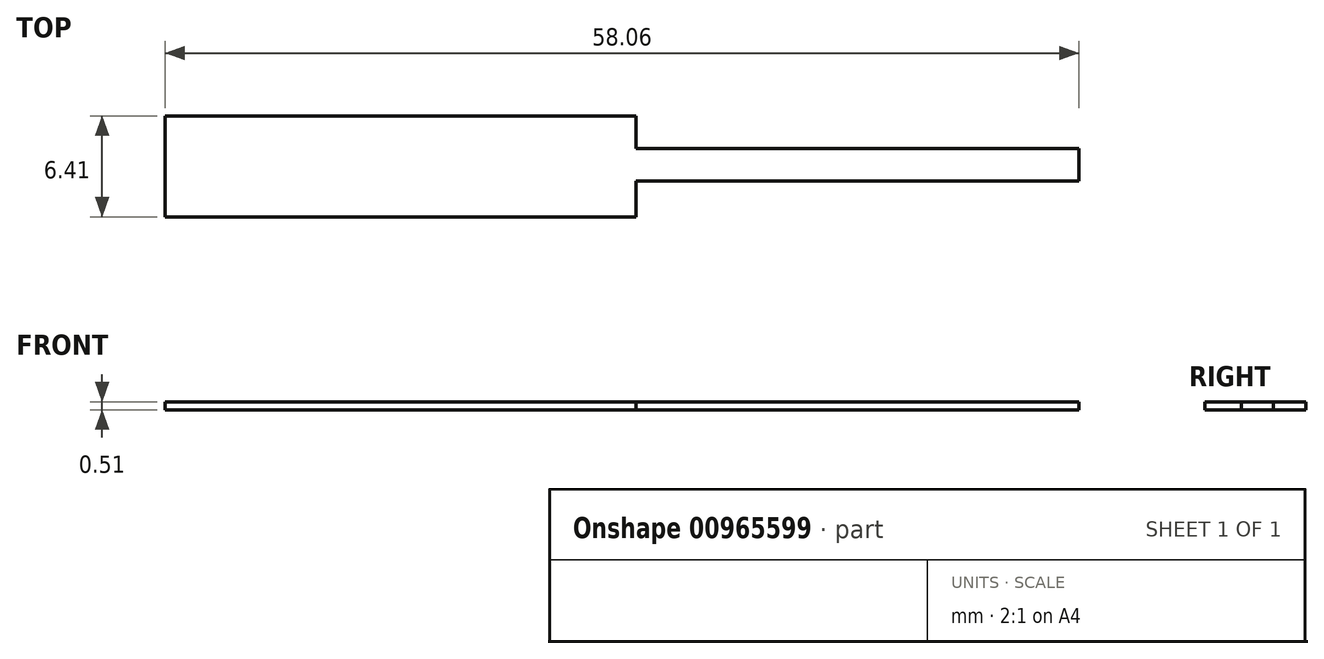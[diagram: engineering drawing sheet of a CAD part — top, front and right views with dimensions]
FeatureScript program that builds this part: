
annotation { "Feature Type Name" : "Feature", "Feature Type Description" : "" }
export const myFeature = defineFeature(function(context is Context, id is Id, definition is map)
    precondition{}
    {
        {
            var Q0;
            Q0=qCreatedBy(makeId("Top.planeOp"),FACE);
            var sketch = newSketch(context, id + "F0", { "sketchPlane" : qUnion([Q0])});
            skLineSegment(sketch, "E0.bottom", {"start": v(-61.27, 31.78) * mm, "end": v(-31.35, 31.78) * mm});
            skLineSegment(sketch, "E0.top", {"start": v(-61.27, 38.19) * mm, "end": v(-31.35, 38.19) * mm});
            skLineSegment(sketch, "E0.left", {"start": v(-61.27, 31.78) * mm, "end": v(-61.27, 38.19) * mm});
            skLineSegment(sketch, "E0.right", {"start": v(-31.35, 31.78) * mm, "end": v(-31.35, 38.19) * mm});
            skLineSegment(sketch, "E1.bottom", {"start": v(-31.35, 36.1) * mm, "end": v(-3.21, 36.1) * mm});
            skLineSegment(sketch, "E1.top", {"start": v(-31.35, 34.07) * mm, "end": v(-3.21, 34.07) * mm});
            skLineSegment(sketch, "E1.left", {"start": v(-31.35, 36.1) * mm, "end": v(-31.35, 34.07) * mm});
            skLineSegment(sketch, "E1.right", {"start": v(-3.21, 36.1) * mm, "end": v(-3.21, 34.07) * mm});
            skSolve(sketch);
        }
        {
            var Q0;
            {var subQ0=sQuery(id+"F0.wireOp",EDGE,"E1.bottom");var subQ6=sQuery(id+"F0.wireOp",EDGE,"E0.bottom");Q0=qUnion([makeQuery(id+"F0.imprint","IMPRINT",FACE,{"disambiguationData":[TD([[makeQuery(id+"F0.imprint","IMPRINT",EDGE,{"derivedFrom":subQ6}),1.0]])]}),makeQuery(id+"F0.imprint","IMPRINT",FACE,{"disambiguationData":[TD([[makeQuery(id+"F0.imprint","IMPRINT",EDGE,{"derivedFrom":subQ0}),-1.0]])]})]);}
            extrude(context, id + "F1", {"entities" : qUnion([Q0]), "depth" : 0.5 * mm, "offsetDistance" : 25.4 * mm});
        }
    });
